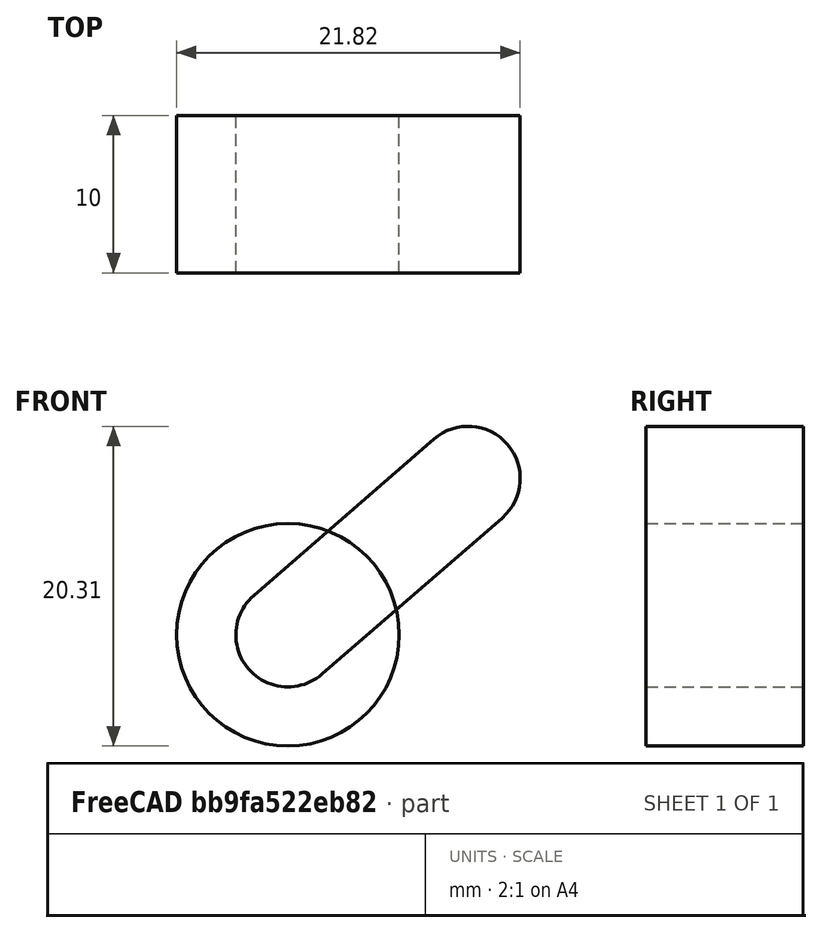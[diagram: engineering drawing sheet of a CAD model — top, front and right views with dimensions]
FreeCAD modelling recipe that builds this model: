
FCSTD DOCUMENT  (FreeCAD 1.1R14555 (Git shallow))
Label: TestInsert1-1
License: All rights reserved
LicenseURL: https://en.wikipedia.org/wiki/All_rights_reserved
objects: App::Point×3, Sketcher::SketchObject×2, PartDesign::Pad×2, PartDesign::Body×2, App::FeaturePython×1, Assembly::JointGroup×1, Assembly::AssemblyObject×1
note: 12 computed .brp shape members not serialized (recipe doc carries the construction recipe); baked Part::Feature solids carry a one-line shape summary decoded from their .brp

FEATURE [App::Point] Origin001  label="Origine"
  Role = Origin
FEATURE [App::Point] Origin003  label="Origine002"
  Role = Origin
FEATURE [Sketcher::SketchObject] Sketch
  ArcFitTolerance = 1e-06
  AttachmentSupport = -> [Origin002]
  ExternalTypes = [0]
  FullyConstrained = false
  MakeInternals = false
  MapMode = 5
  Placement = pos=(0,0,0) rot=(1,0,0;1.5708rad)
  sketch-geometry (4):
    g0: ArcOfCircle CenterX=0 CenterY=0 CenterZ=0 NormalX=0 NormalY=0 NormalZ=1 AngleXU=0 Radius=3.30838 StartAngle=2.28574 EndAngle=5.42733
    g1: ArcOfCircle CenterX=11.4427 CenterY=9.93411 CenterZ=0 NormalX=0 NormalY=0 NormalZ=1 AngleXU=0 Radius=3.30838 StartAngle=5.42733 EndAngle=8.56893
    g2: LineSegment StartX=-2.1689 StartY=2.49826 StartZ=0 EndX=9.27378 EndY=12.4324 EndZ=0
    g3: LineSegment StartX=2.1689 StartY=-2.49826 StartZ=0 EndX=13.6116 EndY=7.43585 EndZ=0
  constraints (6):
    c: Tangent(g0,g2) = 1.5708
    c: Tangent(g0,g3) = -1.5708
    c: Tangent(g1,g2) = 1.5708
    c: Tangent(g1,g3) = -1.5708
    c: Equal(g0,g1)
    c: Coincident(g0,g-1)
FEATURE [PartDesign::Pad] Pad
  Direction = (0,-1,0)
  Length = 10
  Length2 = 10
  Profile = -> Sketch
  ReferenceAxis = -> Sketch [N_Axis]
  Refine = true
  SideType = 0
  Suppressed = false
  Type = 0
  Type2 = 0
FEATURE [PartDesign::Body] Body  label="Corps"
  AllowCompound = false
  Group = -> [Sketch,Pad]
  Origin = -> Origin002
  Tip = -> Pad
FEATURE [App::Point] Origin005  label="Origine004"
  Role = Origin
FEATURE [Sketcher::SketchObject] Sketch001
  ArcFitTolerance = 1e-06
  AttachmentSupport = -> [Origin004]
  ExternalTypes = [0]
  FullyConstrained = false
  MakeInternals = false
  MapMode = 5
  Placement = pos=(0,0,0) rot=(1,0,0;1.5708rad)
  sketch-geometry (1):
    g0: Circle CenterX=0 CenterY=0 CenterZ=0 NormalX=0 NormalY=0 NormalZ=1 AngleXU=0 Radius=7.06658
  constraints (1):
    c: Coincident(g0,g-1)
FEATURE [PartDesign::Pad] Pad001
  Direction = (0,-1,0)
  Length = 10
  Length2 = 10
  Profile = -> Sketch001
  ReferenceAxis = -> Sketch001 [N_Axis]
  Refine = true
  SideType = 0
  Suppressed = false
  Type = 0
  Type2 = 0
FEATURE [PartDesign::Body] Body001  label="Corps001"
  AllowCompound = false
  Group = -> [Sketch001,Pad001]
  Origin = -> Origin004
  Placement = pos=(-4.1e-15,3.6e-15,-4.7e-15) rot=(0,-1,0;4.71239rad)
  Tip = -> Pad001
FEATURE [App::FeaturePython] Joint  label="Fixed"  # Assembly joint (typed FeaturePython)
  Angle = 0
  AngleMax = 0
  AngleMin = 0
  Detach1 = false
  Detach2 = false
  Distance = 0
  Distance2 = 0
  EnableAngleMax = false
  EnableAngleMin = false
  EnableLengthMax = false
  EnableLengthMin = false
  JointType = 0 (Fixed)
  LengthMax = 0
  LengthMin = 0
  Placement1 = pos=(9e-16,-10,2.2e-15) rot=(0.57735,0.57735,0.57735;4.18879rad)
  Placement2 = pos=(0,-10,2.2e-15) rot=(1,0,0;1.5708rad)
  Reference1 = -> Assembly [Body001.Face3,Body001.Face3]
  Reference2 = -> Assembly [Body.Edge4,Body.Edge4]
  Suppressed = false
FEATURE [Assembly::JointGroup] Joints
  Group = -> [Joint]
FEATURE [Assembly::AssemblyObject] Assembly
  Group = -> [Joints,Body,Body001,Joint]
  Origin = -> Origin
  Type = Assembly
